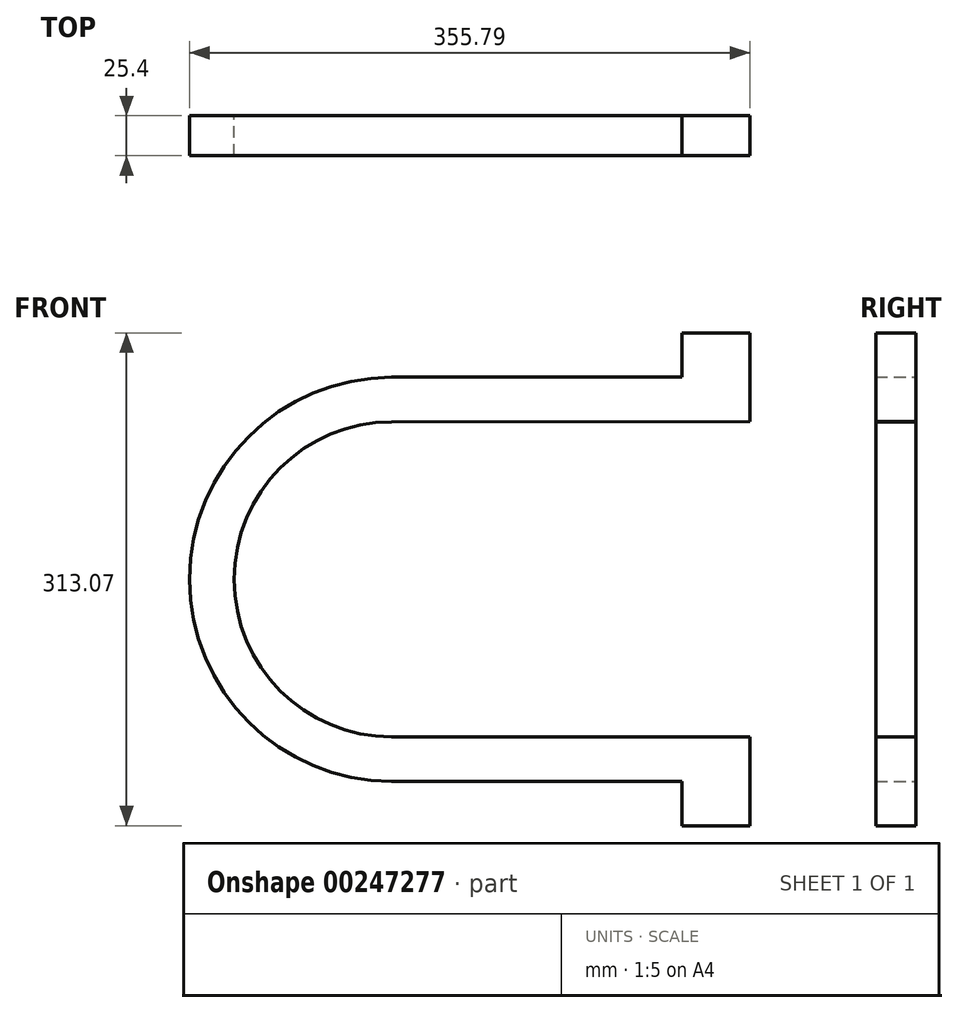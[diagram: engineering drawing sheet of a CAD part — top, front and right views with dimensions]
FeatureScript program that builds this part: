
annotation { "Feature Type Name" : "Feature", "Feature Type Description" : "" }
export const myFeature = defineFeature(function(context is Context, id is Id, definition is map)
    precondition{}
    {
        {
            var Q0;
            Q0=qCreatedBy(makeId("Front.planeOp"),FACE);
            var sketch = newSketch(context, id + "F0", { "sketchPlane" : qUnion([Q0])});
            skArc(sketch, "E0", {"start": v(-15.48, -100.24) * mm, "mid": v(-14.51, -100.25) * mm, "end": v(-13.55, -100.24) * mm});
            skLineSegment(sketch, "E1.top", {"start": v(3.51, -128.44) * mm, "end": v(187.78, -128.44) * mm});
            skLineSegment(sketch, "E1.right", {"start": v(230.96, -100.24) * mm, "end": v(230.96, -128.44) * mm});
            skLineSegment(sketch, "E2.top", {"start": v(3.51, 128.25) * mm, "end": v(187.78, 128.25) * mm});
            skLineSegment(sketch, "E2.right", {"start": v(230.96, 100.05) * mm, "end": v(230.96, 128.25) * mm});
            skLineSegment(sketch, "E3.top", {"start": v(230.96, -156.63) * mm, "end": v(187.78, -156.63) * mm});
            skLineSegment(sketch, "E3.left", {"start": v(230.96, -128.44) * mm, "end": v(230.96, -156.63) * mm});
            skLineSegment(sketch, "E3.right", {"start": v(187.78, -128.44) * mm, "end": v(187.78, -156.63) * mm});
            skLineSegment(sketch, "E4.top", {"start": v(230.96, 156.44) * mm, "end": v(187.78, 156.44) * mm});
            skLineSegment(sketch, "E4.left", {"start": v(230.96, 128.25) * mm, "end": v(230.96, 156.44) * mm});
            skLineSegment(sketch, "E4.right", {"start": v(187.78, 128.25) * mm, "end": v(187.78, 156.44) * mm});
            skLineSegment(sketch, "E5", {"start": v(3.51, 99.97) * mm, "end": v(230.96, 100.05) * mm});
            skLineSegment(sketch, "E6.trimOffspring", {"start": v(3.51, -100.24) * mm, "end": v(230.96, -100.24) * mm});
            skArc(sketch, "E7", {"start": v(3.51, 128.25) * mm, "mid": v(-124.83, -0.1) * mm, "end": v(3.51, -128.44) * mm});
            skArc(sketch, "E8", {"start": v(3.51, 99.97) * mm, "mid": v(-96.6, -0.14) * mm, "end": v(3.51, -100.24) * mm});
            skSolve(sketch);
        }
        {
            var Q0;
            {var subQ1=sQuery(id+"F0.wireOp",EDGE,"NCdKsJzF-0r0Y-WoC2-mI91-WGzqDMnxxrzu");Q0=makeQuery(id+"F0.imprint","IMPRINT",FACE,{"disambiguationData":[TD([[makeQuery(id+"F0.imprint","IMPRINT",EDGE,{"derivedFrom":subQ1}),1.0]])]});}
            var Q1;
            Q1=makeQuery(id+"F0.imprint","IMPRINT",FACE,{"disambiguationData":[TD([[makeQuery(id+"F0.imprint","IMPRINT",EDGE,{"derivedFrom":sQuery(id+"F0.wireOp",EDGE,"E1.top")}),1.0]])]});
            extrude(context, id + "F1", {"entities" : qUnion([Q0, Q1]), "depth" : 25.4 * mm});
        }
    });
